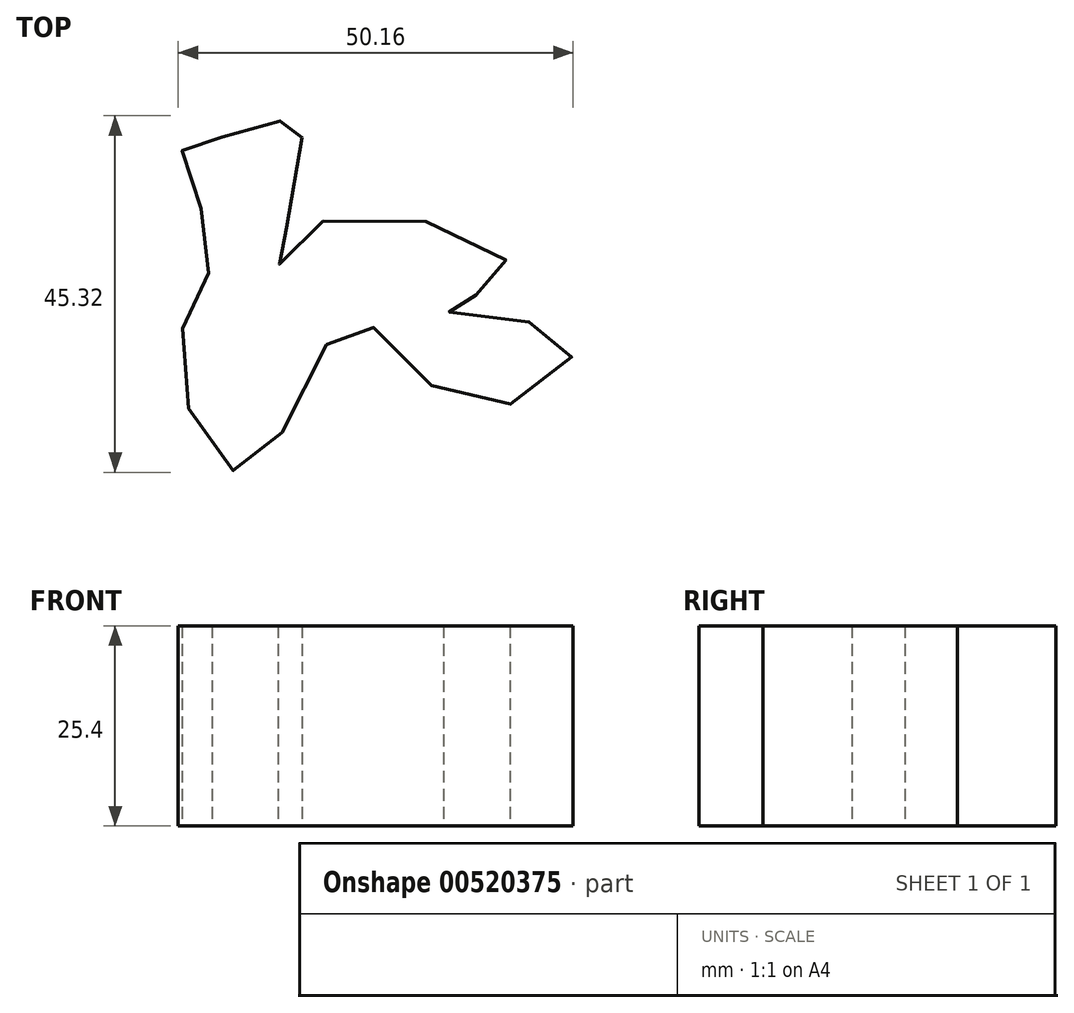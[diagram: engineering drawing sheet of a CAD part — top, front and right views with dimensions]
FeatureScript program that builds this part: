
annotation { "Feature Type Name" : "Feature", "Feature Type Description" : "" }
export const myFeature = defineFeature(function(context is Context, id is Id, definition is map)
    precondition{}
    {
        {
            var Q0;
            Q0=qCreatedBy(makeId("Top.planeOp"),FACE);
            var sketch = newSketch(context, id + "F0", { "sketchPlane" : qUnion([Q0])});
            skFitSpline(sketch, "E0", {"points": [v(-32.86, 40) * mm, v(-32.86, 27.96) * mm, v(-15.92, 29.8) * mm, v(-15.72, 15.3) * mm, v(-32.25, 15.1) * mm, v(-36.94, 0) * mm, v(-19.4, 0) * mm, v(-10.2, 12.65) * mm, v(0, 35.92) * mm, v(-14.9, 46.13) * mm, v(-21.64, 41.03) * mm, v(-35.31, 48.78) * mm, v(-44.3, 43.68) * mm, v(-41.03, 35.31) * mm, v(-35.51, 41.23) * mm, v(-32.04, 45.1) * mm, v(-28.37, 41.03) * mm, v(-32.86, 40) * mm]});
            skSolve(sketch);
        }
        {
            var Q0;
            Q0=sQuery(id+"F0.wireOp",EDGE,"E0");
            extrude(context, id + "F1", {"bodyType" : ToolBodyType.SURFACE, "surfaceEntities" : qUnion([Q0]), "depth" : 25.4 * mm, "offsetDistance" : 25.4 * mm});
        }
        {
            var Q0;
            Q0=qCreatedBy(makeId("Top.planeOp"),FACE);
            var sketch = newSketch(context, id + "F2", { "sketchPlane" : qUnion([Q0])});
            skFitSpline(sketch, "E1", {"points": [v(25.72, 28.37) * mm, v(49.4, 21.84) * mm, v(41.03, 17.15) * mm, v(57.15, 13.27) * mm, v(44.7, 4.7) * mm, v(29.19, 15.72) * mm, v(16.12, -3.47) * mm, v(7.35, 11.84) * mm, v(11.63, 24.5) * mm, v(7.96, 37.76) * mm, v(16.94, 39.6) * mm, v(22.86, 41.23) * mm, v(20, 22.66) * mm, v(25.72, 28.37) * mm]});
            skSolve(sketch);
        }
        {
            var Q0;
            Q0=makeQuery(id+"F2.imprint","IMPRINT",FACE,{"disambiguationData":[TD([[makeQuery(id+"F2.imprint","IMPRINT",EDGE,{"derivedFrom":sQuery(id+"F2.wireOp",EDGE,"E1")}),-1.0]])]});
            extrude(context, id + "F3", {"entities" : qUnion([Q0]), "depth" : 25.4 * mm, "offsetDistance" : 25.4 * mm});
        }
    });
